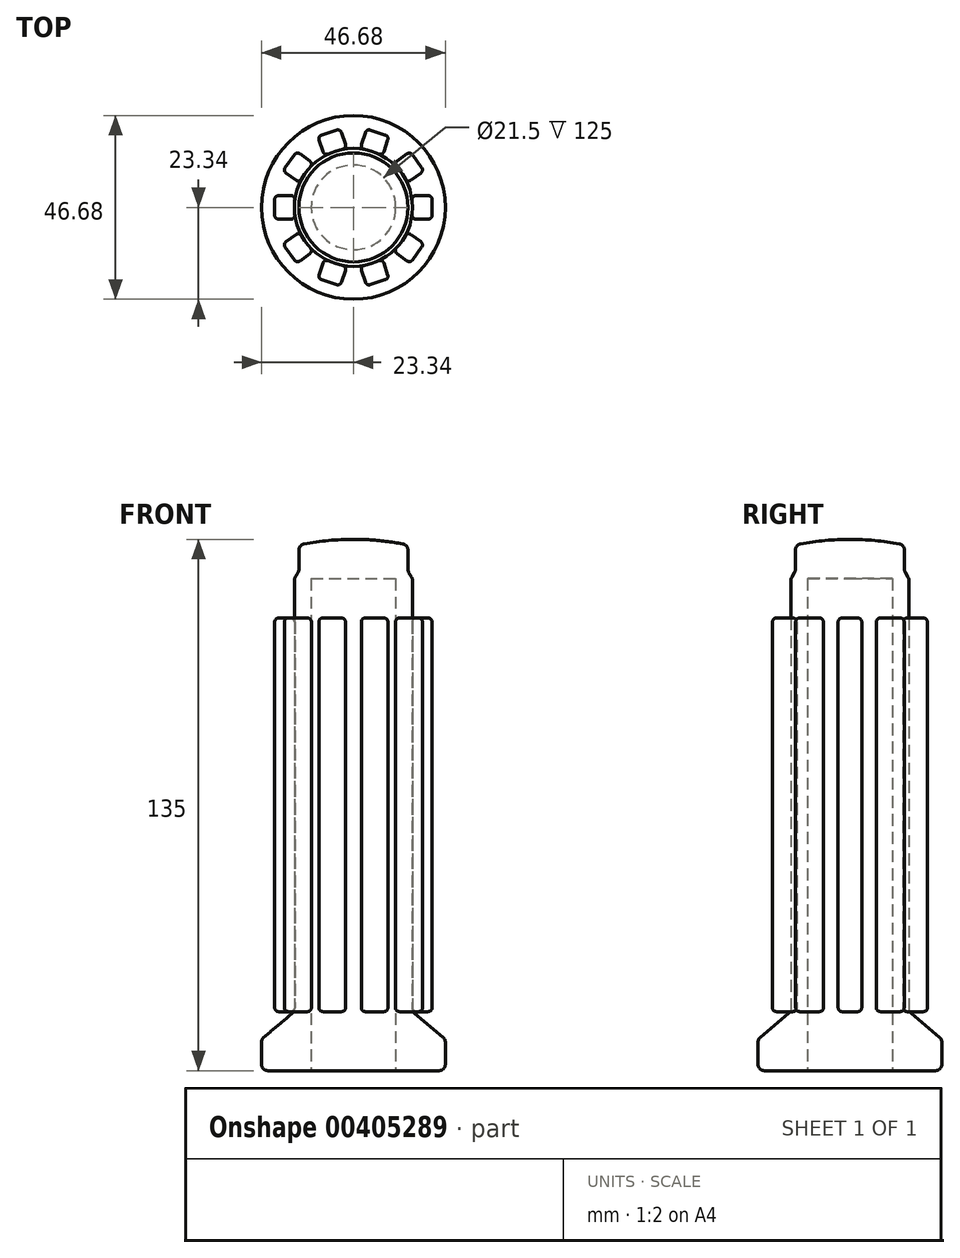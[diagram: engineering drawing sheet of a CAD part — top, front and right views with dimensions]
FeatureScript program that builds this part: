
annotation { "Feature Type Name" : "Feature", "Feature Type Description" : "" }
export const myFeature = defineFeature(function(context is Context, id is Id, definition is map)
    precondition{}
    {
        {
            var Q0;
            Q0=qCreatedBy(makeId("Front.planeOp"),FACE);
            var sketch = newSketch(context, id + "F0", { "sketchPlane" : qUnion([Q0])});
            skLineSegment(sketch, "E0", {"start": v(0, 135) * mm, "end": v(0, 125) * mm});
            skLineSegment(sketch, "E1", {"start": v(0, 125) * mm, "end": v(10.75, 125) * mm});
            skLineSegment(sketch, "E2", {"start": v(10.75, 125) * mm, "end": v(10.75, 0) * mm});
            skLineSegment(sketch, "E3", {"start": v(10.75, 0) * mm, "end": v(23.34, 0) * mm});
            skLineSegment(sketch, "E4", {"start": v(23.34, 0) * mm, "end": v(23.34, 8) * mm});
            skLineSegment(sketch, "E5", {"start": v(23.34, 8) * mm, "end": v(15, 15) * mm});
            skLineSegment(sketch, "E6", {"start": v(15, 15) * mm, "end": v(15, 125) * mm});
            skLineSegment(sketch, "E7", {"start": v(15, 125) * mm, "end": v(13.85, 127) * mm});
            skLineSegment(sketch, "E8", {"start": v(13.85, 127) * mm, "end": v(13.85, 133.58) * mm});
            skArc(sketch, "E9", {"start": v(13.85, 133.58) * mm, "mid": v(6.96, 134.64) * mm, "end": v(0, 135) * mm});
            skLineSegment(sketch, "E10", {"start": v(0, 0) * mm, "end": v(0, 67) * mm, "construction": true});
            skSolve(sketch);
        }
        {
            var Q0;
            Q0=makeQuery(id+"F0.imprint","IMPRINT",FACE,{"disambiguationData":[TD([[makeQuery(id+"F0.imprint","IMPRINT",EDGE,{"derivedFrom":sQuery(id+"F0.wireOp",EDGE,"E0")}),1.0]])]});
            var Q1;
            Q1=sQuery(id+"F0.wireOp",EDGE,"E10");
            revolve(context, id + "F1", {"entities" : qUnion([Q0]), "axis" : qUnion([Q1]), "revolveType" : RevolveType.FULL});
        }
        {
            var Q0;
            Q0=makeQuery(id+"F1.opRevolve","SWEPT_EDGE",EDGE,{"disambiguationData":[OSD([sQuery(id+"F0.wireOp",EDGE,"E8"),sQuery(id+"F0.wireOp",EDGE,"E9")])]});
            var Q1;
            Q1=makeQuery(id+"F1.opRevolve","SWEPT_EDGE",EDGE,{"disambiguationData":[OSD([sQuery(id+"F0.wireOp",EDGE,"E7"),sQuery(id+"F0.wireOp",EDGE,"E8")])]});
            var Q2;
            Q2=makeQuery(id+"F1.opRevolve","SWEPT_EDGE",EDGE,{"disambiguationData":[OSD([sQuery(id+"F0.wireOp",EDGE,"E6"),sQuery(id+"F0.wireOp",EDGE,"E7")])]});
            var Q3;
            Q3=makeQuery(id+"F1.opRevolve","SWEPT_EDGE",EDGE,{"disambiguationData":[OSD([sQuery(id+"F0.wireOp",EDGE,"E5"),sQuery(id+"F0.wireOp",EDGE,"E6")])]});
            var Q4;
            Q4=makeQuery(id+"F1.opRevolve","SWEPT_EDGE",EDGE,{"disambiguationData":[OSD([sQuery(id+"F0.wireOp",EDGE,"E4"),sQuery(id+"F0.wireOp",EDGE,"E5")])]});
            var Q5;
            Q5=makeQuery(id+"F1.opRevolve","SWEPT_EDGE",EDGE,{"disambiguationData":[OSD([sQuery(id+"F0.wireOp",EDGE,"E3"),sQuery(id+"F0.wireOp",EDGE,"E4")])]});
            fillet(context, id + "F2", {"entities" : qUnion([Q0, Q1, Q2, Q3, Q4, Q5]), "radius" : 1.6 * mm, "tangentPropagation" : true, "allowEdgeOverflow" : false});
        }
        {
            var Q0;
            Q0=qCreatedBy(makeId("Right.planeOp"),FACE);
            cPlane(context, id + "F3", {"entities" : qUnion([Q0]), "cplaneType" : CPlaneType.OFFSET, "offset" : 20 * mm, "width" : 150 * mm, "height" : 150 * mm});
        }
        {
            var Q0;
            Q0=qCreatedBy(id+"F3.planeOp",FACE);
            var sketch = newSketch(context, id + "F4", { "sketchPlane" : qUnion([Q0])});
            skLineSegment(sketch, "E11.bottom", {"start": v(-3, 115) * mm, "end": v(3, 115) * mm});
            skLineSegment(sketch, "E11.top", {"start": v(-3, 15) * mm, "end": v(3, 15) * mm});
            skLineSegment(sketch, "E11.left", {"start": v(-3, 115) * mm, "end": v(-3, 15) * mm});
            skLineSegment(sketch, "E11.right", {"start": v(3, 115) * mm, "end": v(3, 15) * mm});
            skSolve(sketch);
        }
        {
            var Q0;
            Q0=makeQuery(id+"F4.imprint","IMPRINT",FACE,{"disambiguationData":[TD([[makeQuery(id+"F4.imprint","IMPRINT",EDGE,{"derivedFrom":sQuery(id+"F4.wireOp",EDGE,"E11.bottom")}),-1.0]])]});
            var Q1;
            Q1=makeQuery(id+"F1.opRevolve","SWEPT_FACE",FACE,{"disambiguationData":[OSD([sQuery(id+"F0.wireOp",EDGE,"E6")])]});
            extrude(context, id + "F5", {"entities" : qUnion([Q0]), "endBound" : BoundingType.UP_TO_SURFACE, "oppositeDirection" : true, "endBoundEntityFace" : qUnion([Q1]), "depth" : 25 * mm});
        }
        {
            var Q0;
            Q0=makeQuery(id+"F5.opExtrude","SWEPT_EDGE",EDGE,{"disambiguationData":[OSD([sQuery(id+"F4.wireOp",EDGE,"E11.bottom"),sQuery(id+"F4.wireOp",EDGE,"E11.right")])]});
            var Q1;
            Q1=makeQuery(id+"F5.opExtrude","SWEPT_EDGE",EDGE,{"disambiguationData":[OSD([sQuery(id+"F4.wireOp",EDGE,"E11.bottom"),sQuery(id+"F4.wireOp",EDGE,"E11.left")])]});
            var Q2;
            Q2=makeQuery(id+"F5.opExtrude","CAP_EDGE",EDGE,{"disambiguationData":[OSD([sQuery(id+"F4.wireOp",EDGE,"E11.left")])],"isStart":true});
            var Q3;
            Q3=makeQuery(id+"F5.opExtrude","CAP_EDGE",EDGE,{"disambiguationData":[OSD([sQuery(id+"F4.wireOp",EDGE,"E11.right")])],"isStart":true});
            var Q4;
            Q4=makeQuery(id+"F5.opExtrude","CAP_EDGE",EDGE,{"disambiguationData":[OSD([sQuery(id+"F4.wireOp",EDGE,"E11.right")])],"isStart":false});
            var Q5;
            Q5=makeQuery(id+"F5.opExtrude","CAP_EDGE",EDGE,{"disambiguationData":[OSD([sQuery(id+"F4.wireOp",EDGE,"E11.left")])],"isStart":false});
            var Q6;
            Q6=makeQuery(id+"F5.opExtrude","SWEPT_EDGE",EDGE,{"disambiguationData":[OSD([sQuery(id+"F4.wireOp",EDGE,"E11.top"),sQuery(id+"F4.wireOp",EDGE,"E11.right")])]});
            var Q7;
            Q7=makeQuery(id+"F5.opExtrude","CAP_EDGE",EDGE,{"disambiguationData":[OSD([sQuery(id+"F4.wireOp",EDGE,"E11.top")])],"isStart":true});
            var Q8;
            Q8=makeQuery(id+"F5.opExtrude","SWEPT_FACE",FACE,{"disambiguationData":[OSD([sQuery(id+"F4.wireOp",EDGE,"E11.top")])]});
            var Q9;
            Q9=makeQuery(id+"F5.opExtrude","SWEPT_EDGE",EDGE,{"disambiguationData":[OSD([sQuery(id+"F4.wireOp",EDGE,"E11.top"),sQuery(id+"F4.wireOp",EDGE,"E11.left")])]});
            var Q10;
            Q10=makeQuery(id+"F5.opExtrude","CAP_EDGE",EDGE,{"disambiguationData":[OSD([sQuery(id+"F4.wireOp",EDGE,"E11.bottom")])],"isStart":false});
            var Q11;
            Q11=makeQuery(id+"F5.opExtrude","CAP_EDGE",EDGE,{"disambiguationData":[OSD([sQuery(id+"F4.wireOp",EDGE,"E11.bottom")])],"isStart":true});
            fillet(context, id + "F6", {"entities" : qUnion([Q0, Q1, Q2, Q3, Q4, Q5, Q6, Q7, Q8, Q9, Q10, Q11]), "radius" : 1 * mm, "tangentPropagation" : true, "allowEdgeOverflow" : false});
        }
        {
            var Q0;
            Q0=makeQuery(id+"F5.opExtrude","SWEPT_BODY",BODY,{"disambiguationData":[OSD([sQuery(id+"F4.wireOp",EDGE,"E11.bottom"),sQuery(id+"F4.wireOp",EDGE,"E11.top"),sQuery(id+"F4.wireOp",EDGE,"E11.left"),sQuery(id+"F4.wireOp",EDGE,"E11.right")])]});
            var Q1;
            Q1=sQuery(id+"F0.wireOp",EDGE,"E10");
            circularPattern(context, id + "F7", {"entities" : qUnion([Q0]), "axis" : qUnion([Q1]), "angle" : 360 * degree, "instanceCount" : 10, "equalSpace" : true});
        }
    });
